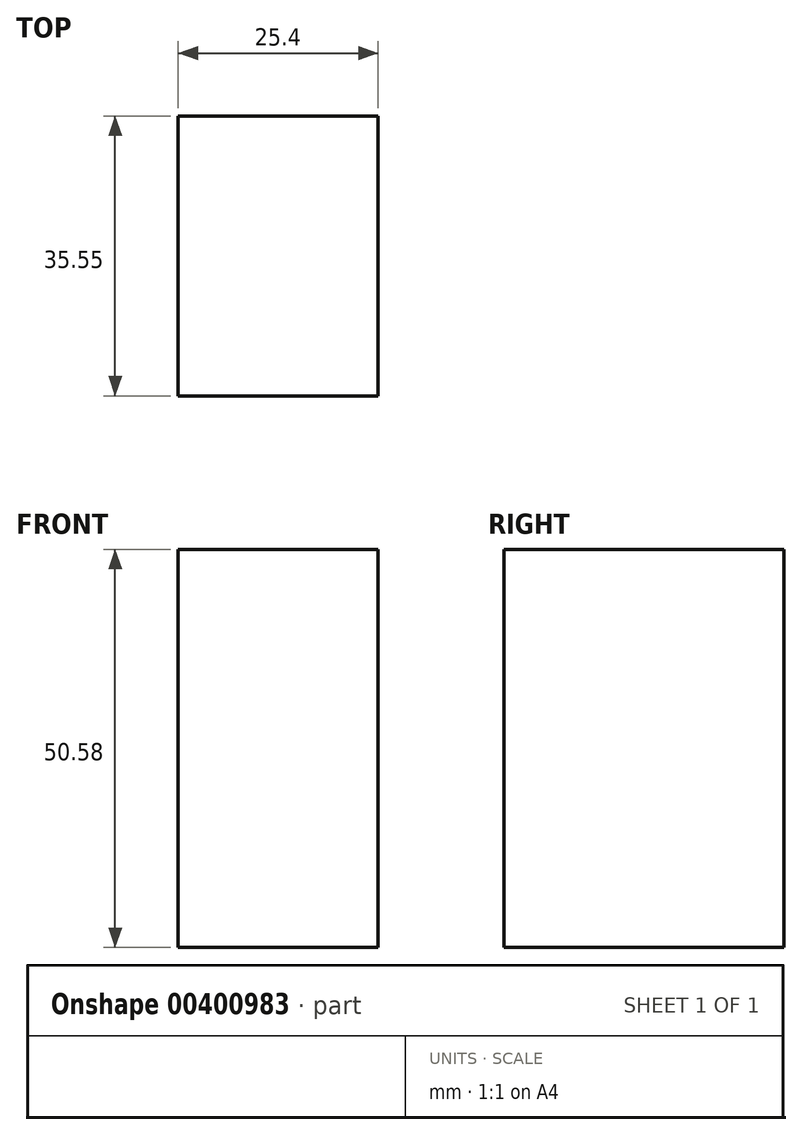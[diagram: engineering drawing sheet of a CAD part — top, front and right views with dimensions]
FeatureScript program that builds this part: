
annotation { "Feature Type Name" : "Feature", "Feature Type Description" : "" }
export const myFeature = defineFeature(function(context is Context, id is Id, definition is map)
    precondition{}
    {
        {
            var Q0;
            Q0=qCreatedBy(makeId("Right.planeOp"),FACE);
            var sketch = newSketch(context, id + "F0", { "sketchPlane" : qUnion([Q0])});
            skLineSegment(sketch, "E0.bottom", {"start": v(59.27, 0) * mm, "end": v(23.72, 0) * mm});
            skLineSegment(sketch, "E0.top", {"start": v(59.27, -50.58) * mm, "end": v(23.72, -50.58) * mm});
            skLineSegment(sketch, "E0.left", {"start": v(59.27, 0) * mm, "end": v(59.27, -50.58) * mm});
            skLineSegment(sketch, "E0.right", {"start": v(23.72, 0) * mm, "end": v(23.72, -50.58) * mm});
            skSolve(sketch);
        }
        {
            var Q0;
            Q0 = qSketchRegion(id + "F0", true);
            extrude(context, id + "F1", {"entities" : qUnion([Q0]), "depth" : 25.4 * mm});
        }
    });
